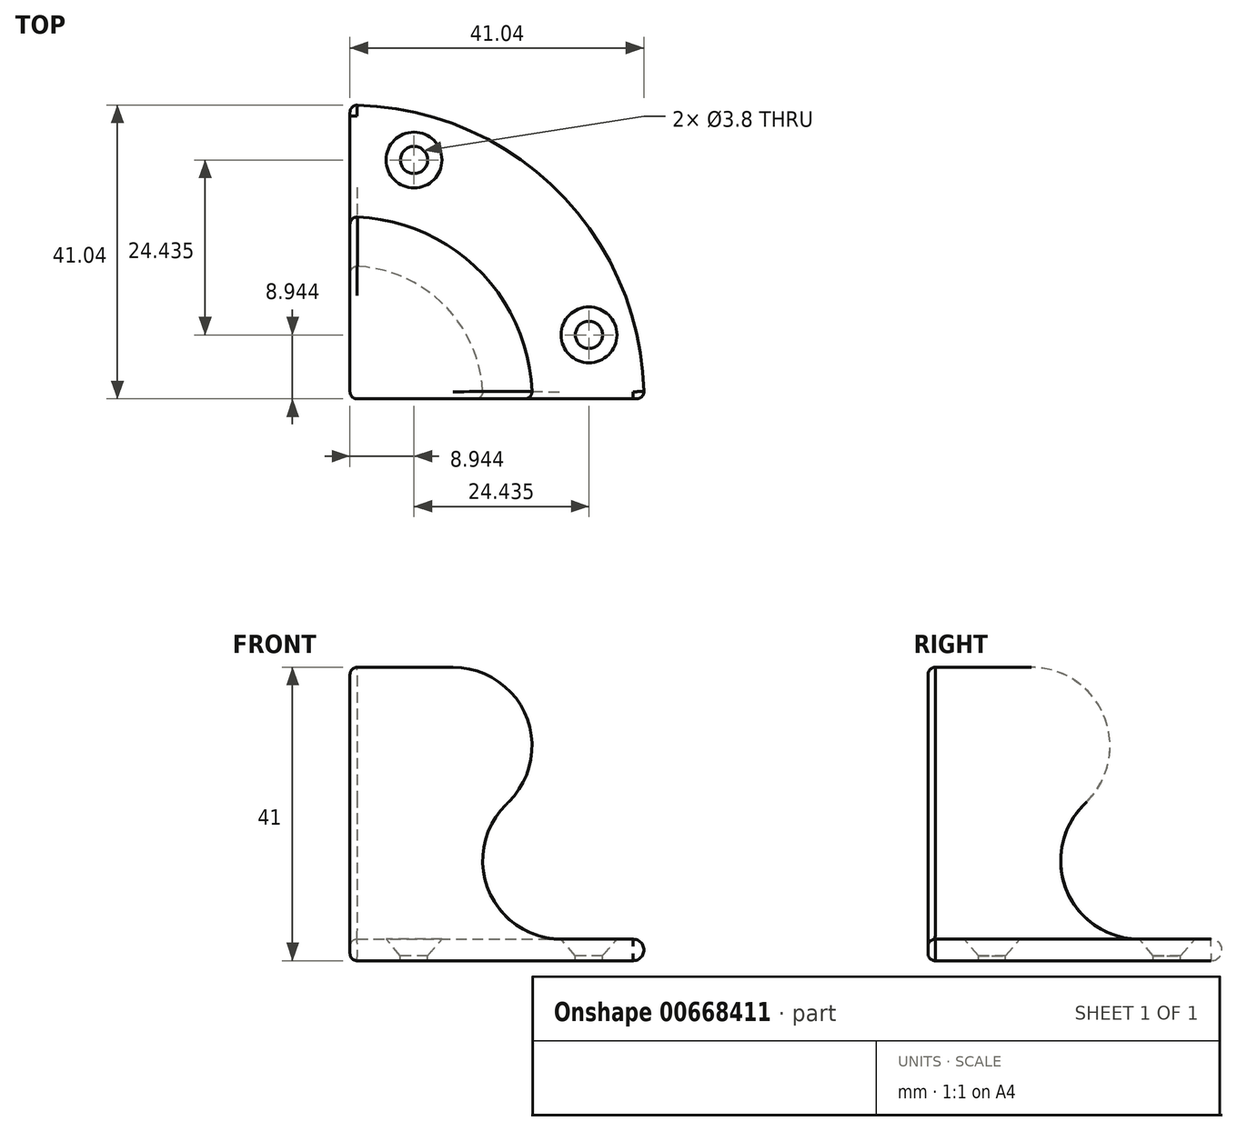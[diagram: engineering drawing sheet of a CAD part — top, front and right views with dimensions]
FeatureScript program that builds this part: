
annotation { "Feature Type Name" : "Feature", "Feature Type Description" : "" }
export const myFeature = defineFeature(function(context is Context, id is Id, definition is map)
    precondition{}
    {
        {
            var Q0;
            Q0=qCreatedBy(makeId("Front.planeOp"),FACE);
            var sketch = newSketch(context, id + "F0", { "sketchPlane" : qUnion([Q0])});
            skLineSegment(sketch, "E0", {"start": v(21.78, 21.78) * mm, "end": v(22.22, 22.22) * mm});
            skLineSegment(sketch, "E1.bottom", {"start": v(0, 0) * mm, "end": v(39.56, 0) * mm});
            skLineSegment(sketch, "E1.top", {"start": v(0, 41) * mm, "end": v(14.44, 41) * mm});
            skLineSegment(sketch, "E1.left", {"start": v(0, 0) * mm, "end": v(0, 41) * mm});
            skLineSegment(sketch, "E2", {"start": v(29.56, 3) * mm, "end": v(39.56, 3) * mm});
            skArc(sketch, "E3", {"start": v(39.56, 3) * mm, "mid": v(41.06, 1.5) * mm, "end": v(39.56, 0) * mm});
            skArc(sketch, "E4", {"start": v(21.78, 21.78) * mm, "mid": v(19.4, 9.8) * mm, "end": v(29.56, 3) * mm});
            skArc(sketch, "E5", {"start": v(22.22, 22.22) * mm, "mid": v(24.6, 34.2) * mm, "end": v(14.44, 41) * mm});
            skPoint(sketch, "E6.visualSharp", {"position": v(0, 41) * mm});
            skPoint(sketch, "E7.visualSharp", {"position": v(0, 0) * mm});
            skSolve(sketch);
        }
        {
            var Q0;
            Q0=makeQuery(id+"F0.imprint","IMPRINT",FACE,{"disambiguationData":[TD([[makeQuery(id+"F0.imprint","IMPRINT",EDGE,{"derivedFrom":sQuery(id+"F0.wireOp",EDGE,"E0")}),1.0]])]});
            var Q1;
            Q1=sQuery(id+"F0.wireOp",EDGE,"E1.left");
            revolve(context, id + "F1", {"entities" : qUnion([Q0]), "axis" : qUnion([Q1]), "revolveType" : RevolveType.ONE_DIRECTION, "angle" : 90 * degree});
        }
        {
            var Q0;
            Q0=makeQuery(id+"F1.opRevolve","SWEPT_FACE",FACE,{"disambiguationData":[OSD([sQuery(id+"F0.wireOp",EDGE,"E2")])]});
            var sketch = newSketch(context, id + "F2", { "sketchPlane" : qUnion([Q0])});
            skLineSegment(sketch, "E8", {"start": v(0, 0) * mm, "end": v(13.01, 48.56) * mm});
            skLineSegment(sketch, "E9", {"start": v(0, 0) * mm, "end": v(60.26, 16.15) * mm});
            skCircle(sketch, "E10", {"center": v(8.94, 33.38) * mm, "radius": 5 * mm});
            skCircle(sketch, "E11", {"center": v(33.38, 8.94) * mm, "radius": 5 * mm});
            skLineSegment(sketch, "E12", {"start": v(0, 0) * mm, "end": v(37.84, 37.84) * mm});
            skSolve(sketch);
        }
        {
            var Q0;
            Q0=sQuery(id+"F2.wireOp",VERTEX,"E10.center");
            var Q1;
            Q1=sQuery(id+"F2.wireOp",VERTEX,"E11.center");
            var Q2;
            Q2=makeQuery(id+"F1.opRevolve","SWEPT_BODY",BODY,{"disambiguationData":[OSD([sQuery(id+"F0.wireOp",EDGE,"E0"),sQuery(id+"F0.wireOp",EDGE,"E1.bottom"),sQuery(id+"F0.wireOp",EDGE,"E1.top"),sQuery(id+"F0.wireOp",EDGE,"E1.left"),sQuery(id+"F0.wireOp",EDGE,"E2"),sQuery(id+"F0.wireOp",EDGE,"E3"),sQuery(id+"F0.wireOp",EDGE,"E4"),sQuery(id+"F0.wireOp",EDGE,"E5"),sQuery(id+"F0.wireOp",EDGE,"E6.filletArc"),sQuery(id+"F0.wireOp",EDGE,"E7.filletArc")])]});
            hole(context, id + "F3", {"style" : HoleStyle.C_SINK, "endStyle" : HoleEndStyle.THROUGH, "standardTappedOrClearance" : lookupTablePath({ "standard" : "ANSI", "fit" : "Normal (ASME)", "size" : "#6", "type" : "Clearance" }), "standardBlindInLast" : lookupTablePath({ "fit" : "Free", "standard" : "ANSI", "size" : "#6", "type" : "Clearance" }), "holeDiameter" : 3.8 * mm, "cSinkDiameter" : 7.8 * mm, "cSinkAngle" : 82 * degree, "majorDiameter" : 5 * mm, "isTappedThrough" : true, "tappedDepth" : 12 * mm, "tapClearance" : 3, "locations" : qUnion([Q0, Q1]), "scope" : qUnion([Q2])});
        }
        {
            var Q0;
            Q0=makeQuery(id+"F1.opRevolve","CAP_FACE",FACE,{"disambiguationData":[OSD([sQuery(id+"F0.wireOp",EDGE,"E0"),sQuery(id+"F0.wireOp",EDGE,"E1.bottom"),sQuery(id+"F0.wireOp",EDGE,"E1.top"),sQuery(id+"F0.wireOp",EDGE,"E1.left"),sQuery(id+"F0.wireOp",EDGE,"E2"),sQuery(id+"F0.wireOp",EDGE,"E3"),sQuery(id+"F0.wireOp",EDGE,"E4"),sQuery(id+"F0.wireOp",EDGE,"E5")])],"isStart":true});
            var Q1;
            Q1=makeQuery(id+"F1.opRevolve","CAP_FACE",FACE,{"disambiguationData":[OSD([sQuery(id+"F0.wireOp",EDGE,"E0"),sQuery(id+"F0.wireOp",EDGE,"E1.bottom"),sQuery(id+"F0.wireOp",EDGE,"E1.top"),sQuery(id+"F0.wireOp",EDGE,"E1.left"),sQuery(id+"F0.wireOp",EDGE,"E2"),sQuery(id+"F0.wireOp",EDGE,"E3"),sQuery(id+"F0.wireOp",EDGE,"E4"),sQuery(id+"F0.wireOp",EDGE,"E5")])],"isStart":false});
            fillet(context, id + "F4", {"entities" : qUnion([Q0, Q1]), "radius" : 1 * mm, "tangentPropagation" : true, "allowEdgeOverflow" : false});
        }
    });
